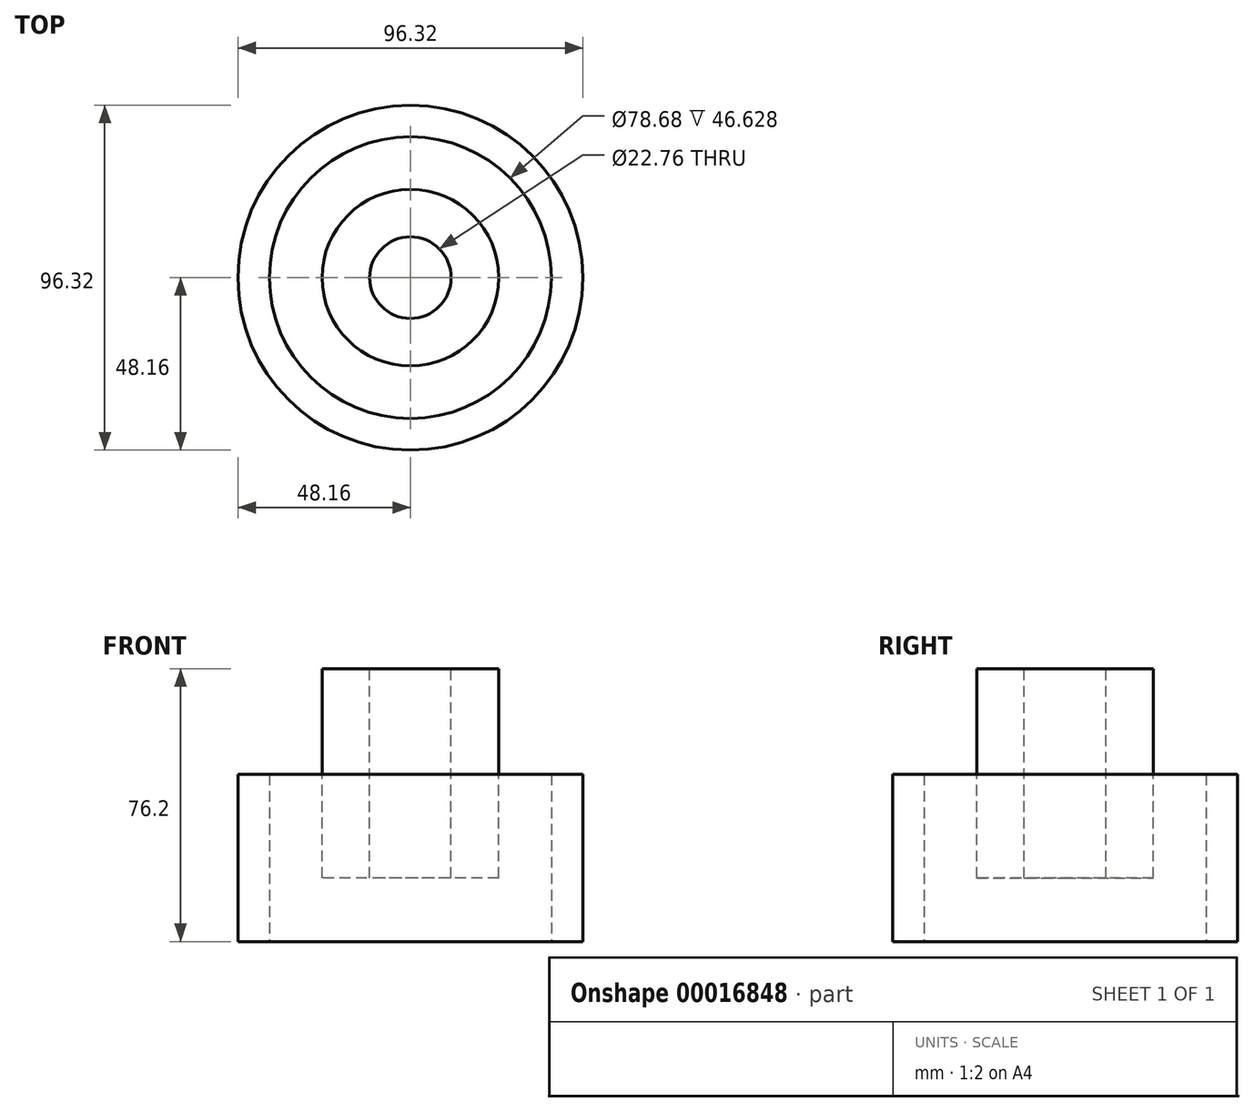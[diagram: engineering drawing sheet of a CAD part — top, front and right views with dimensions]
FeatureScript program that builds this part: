
annotation { "Feature Type Name" : "Feature", "Feature Type Description" : "" }
export const myFeature = defineFeature(function(context is Context, id is Id, definition is map)
    precondition{}
    {
        {
            var Q0;
            Q0=qCreatedBy(makeId("Top.planeOp"),FACE);
            var sketch = newSketch(context, id + "F0", { "sketchPlane" : qUnion([Q0])});
            skCircle(sketch, "E0", {"center": v(0, 0) * mm, "radius": 48.16 * mm});
            skCircle(sketch, "E1", {"center": v(0, 0) * mm, "radius": 39.34 * mm});
            skSolve(sketch);
        }
        {
            var Q0;
            Q0=qCreatedBy(makeId("Top.planeOp"),FACE);
            cPlane(context, id + "F1", {"entities" : qUnion([Q0]), "cplaneType" : CPlaneType.OFFSET, "offset" : 76.2 * mm, "width" : 152.4 * mm, "height" : 152.4 * mm});
        }
        {
            var Q0;
            Q0=qCreatedBy(id+"F1.planeOp",FACE);
            var sketch = newSketch(context, id + "F2", { "sketchPlane" : qUnion([Q0])});
            skPoint(sketch, "E2.rect.middle", {"position": v(0, 0) * mm});
            skCircle(sketch, "E3", {"center": v(0, 0) * mm, "radius": 24.66 * mm});
            skCircle(sketch, "E4", {"center": v(0, 0) * mm, "radius": 11.38 * mm});
            skSolve(sketch);
        }
        {
            var Q0;
            Q0=makeQuery(id+"F0.imprint","IMPRINT",FACE,{"disambiguationData":[TD([[makeQuery(id+"F0.imprint","IMPRINT",EDGE,{"derivedFrom":sQuery(id+"F0.wireOp",EDGE,"E0")}),1.0]])]});
            extrude(context, id + "F3", {"entities" : qUnion([Q0]), "depth" : 46.63 * mm});
        }
        {
            var Q0;
            Q0=makeQuery(id+"F2.imprint","IMPRINT",FACE,{"disambiguationData":[TD([[makeQuery(id+"F2.imprint","IMPRINT",EDGE,{"derivedFrom":sQuery(id+"F2.wireOp",EDGE,"E3")}),1.0]])]});
            extrude(context, id + "F4", {"entities" : qUnion([Q0]), "oppositeDirection" : true, "depth" : 58.43 * mm});
        }
    });
